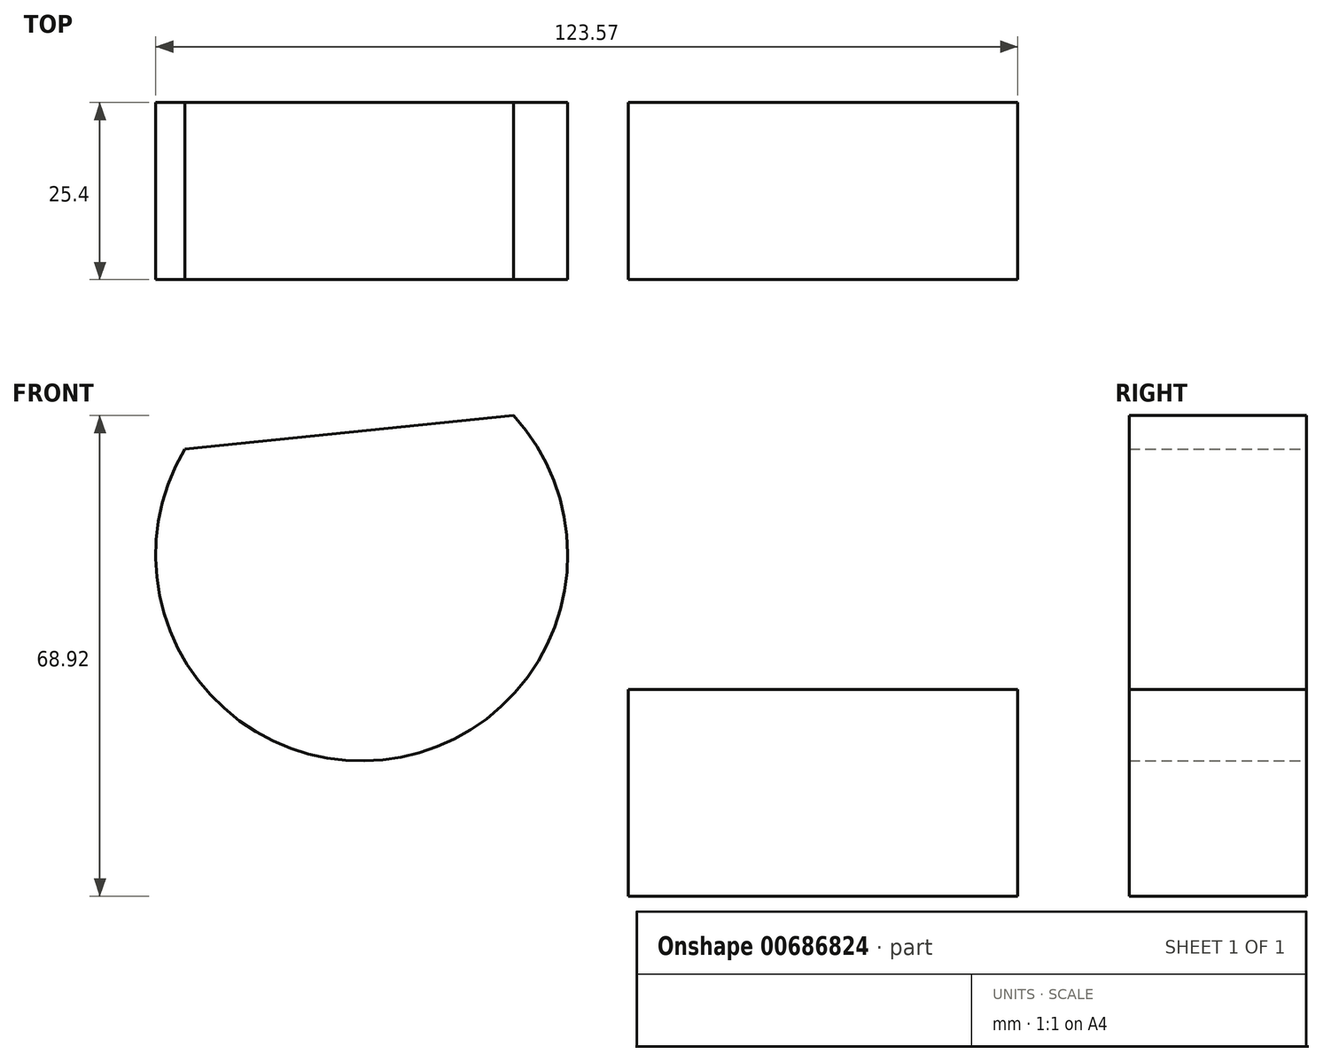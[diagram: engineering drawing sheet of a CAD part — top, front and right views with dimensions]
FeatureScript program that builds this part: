
annotation { "Feature Type Name" : "Feature", "Feature Type Description" : "" }
export const myFeature = defineFeature(function(context is Context, id is Id, definition is map)
    precondition{}
    {
        {
            var Q0;
            Q0=qCreatedBy(makeId("Front.planeOp"),FACE);
            var sketch = newSketch(context, id + "F0", { "sketchPlane" : qUnion([Q0])});
            skArc(sketch, "E0", {"start": v(-88.07, 51.58) * mm, "mid": v(-59.73, 7.02) * mm, "end": v(-41, 56.4) * mm});
            skLineSegment(sketch, "E1.bottom", {"start": v(-24.54, -12.52) * mm, "end": v(31.3, -12.52) * mm});
            skLineSegment(sketch, "E1.top", {"start": v(-24.54, 17.12) * mm, "end": v(31.3, 17.12) * mm});
            skLineSegment(sketch, "E1.left", {"start": v(-24.54, -12.52) * mm, "end": v(-24.54, 17.12) * mm});
            skLineSegment(sketch, "E1.right", {"start": v(31.3, -12.52) * mm, "end": v(31.3, 17.12) * mm});
            skLineSegment(sketch, "E2", {"start": v(-88.07, 51.58) * mm, "end": v(-41, 56.4) * mm});
            skSolve(sketch);
        }
        {
            var Q0;
            Q0 = qSketchRegion(id + "F0", true);
            extrude(context, id + "F1", {"entities" : qUnion([Q0]), "depth" : 25.4 * mm, "offsetDistance" : 25.4 * mm});
        }
    });
